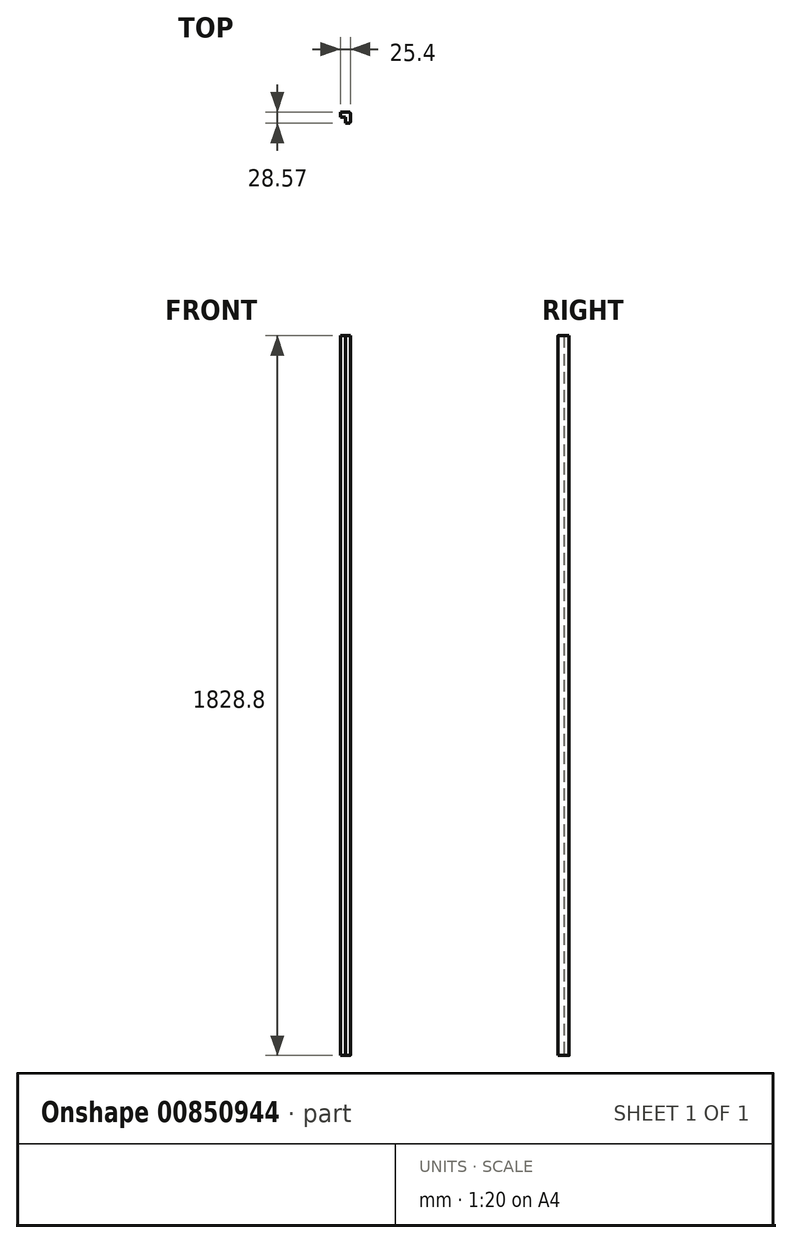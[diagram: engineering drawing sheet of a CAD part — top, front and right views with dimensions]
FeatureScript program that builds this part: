
annotation { "Feature Type Name" : "Feature", "Feature Type Description" : "" }
export const myFeature = defineFeature(function(context is Context, id is Id, definition is map)
    precondition{}
    {
        {
            var Q0;
            Q0=qCreatedBy(makeId("Top.planeOp"),FACE);
            var sketch = newSketch(context, id + "F0", { "sketchPlane" : qUnion([Q0])});
            skLineSegment(sketch, "E0", {"start": v(0, 0) * mm, "end": v(9.53, 0) * mm});
            skLineSegment(sketch, "E1", {"start": v(12.7, 3.18) * mm, "end": v(12.7, 25.4) * mm});
            skLineSegment(sketch, "E2", {"start": v(9.52, 28.57) * mm, "end": v(-12.7, 28.57) * mm});
            skLineSegment(sketch, "E3", {"start": v(-12.7, 28.57) * mm, "end": v(-12.7, 15.87) * mm});
            skLineSegment(sketch, "E4", {"start": v(-12.7, 15.87) * mm, "end": v(0, 15.87) * mm});
            skLineSegment(sketch, "E5", {"start": v(0, 15.87) * mm, "end": v(0, 0) * mm});
            skPoint(sketch, "E6.visualSharp", {"position": v(12.7, 28.58) * mm});
            skArc(sketch, "E6.filletArc", {"start": v(12.7, 25.4) * mm, "mid": v(11.77, 27.65) * mm, "end": v(9.52, 28.57) * mm});
            skPoint(sketch, "E7.visualSharp", {"position": v(12.7, 0) * mm});
            skArc(sketch, "E7.filletArc", {"start": v(9.53, 0) * mm, "mid": v(11.77, 0.93) * mm, "end": v(12.7, 3.18) * mm});
            skSolve(sketch);
        }
        {
            var Q0;
            Q0=makeQuery(id+"F0.imprint","IMPRINT",FACE,{"disambiguationData":[TD([[makeQuery(id+"F0.imprint","IMPRINT",EDGE,{"derivedFrom":sQuery(id+"F0.wireOp",EDGE,"E0")}),1.0]])]});
            extrude(context, id + "F1", {"entities" : qUnion([Q0]), "depth" : 1828.8 * mm, "offsetDistance" : 25.4 * mm});
        }
    });
